# Revit family: PlumbingFixture_Grate_Galvin_G200S-Th
name_source: partatom
category: Plumbing Fixtures
revit_build: Autodesk Revit MEP 2012 (Build: 20110916_2132(x64)
units: mm (PartAtom-declared; Revit-internal decimal feet)

## types (2) — shared parameters
Assembly Code = D2040200
BodyMaterial = Metal_Drains_Stainless-Steel-Threaded_15400
CHWFlow_ANZRS = 6.4 L/s
Circulation_ANZRS = Yes
Description = Square Threaded Floor Drain - Grate Assembly
DimDepth = 40 mm  [stored 0.131234 ft]
DimTop = 200 mm  [stored 0.656168 ft]
FilterObject_ANZRS = GS-Th
GrateMaterial = Metal_Drains_Stainless-Steel_15400
Instructions = http://www.galvinengineering.com.au
Keynote = 10800
Manufacturer = Galvin Engineering
ModifiedIssue_ANZRS = 20140526 $
StyleOrType_ANZRS = Grate
Type Comments = Square
URL = www.galvinengineering.com.au
zero-valued in all types: Default Elevation

## per-type parameters (varying)
| type | DimHeight | DimOutlet | OutletRadius_DoNotEdit |
| 302752X - ST/ST 316 | 76 mm  [stored 0.249344 ft] | 100 mm  [stored 0.328084 ft] | 50 mm  [stored 0.164042 ft] |
| 302756X - ST/ST 316 | 69 mm  [stored 0.226378 ft] | 150 mm | 75 mm |

note: column(s) folded — value = type name in every type: Model

note: [stored X ft] marks values corroborated as IEEE doubles in the binary element streams (Revit-internal decimal feet)

## geometry (parser evidence)
native form markers: Blend x4, Sweep x1
no freeform markers — native parametric forms only
